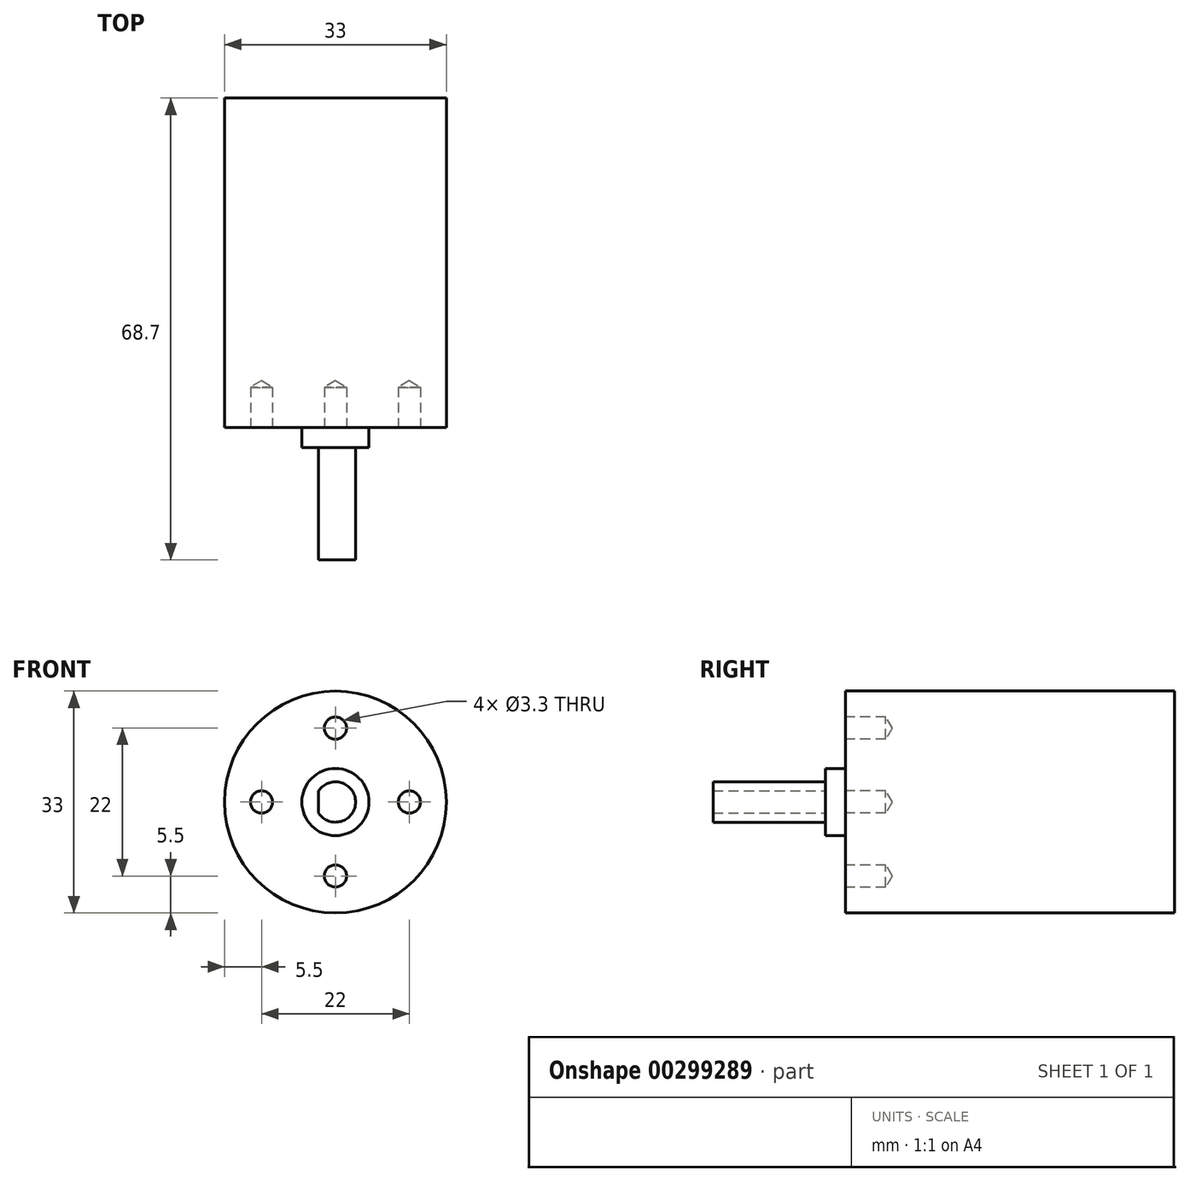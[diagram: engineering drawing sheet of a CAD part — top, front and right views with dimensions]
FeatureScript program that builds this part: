
annotation { "Feature Type Name" : "Feature", "Feature Type Description" : "" }
export const myFeature = defineFeature(function(context is Context, id is Id, definition is map)
    precondition{}
    {
        {
            var Q0;
            Q0=qCreatedBy(makeId("Front.planeOp"),FACE);
            var sketch = newSketch(context, id + "F0", { "sketchPlane" : qUnion([Q0])});
            skCircle(sketch, "E0", {"center": v(0, 0) * mm, "radius": 16.5 * mm});
            skSolve(sketch);
        }
        {
            var Q0;
            Q0=makeQuery(id+"F0.imprint","IMPRINT",FACE,{"disambiguationData":[TD([[makeQuery(id+"F0.imprint","IMPRINT",EDGE,{"derivedFrom":sQuery(id+"F0.wireOp",EDGE,"E0")}),1.0]])]});
            extrude(context, id + "F1", {"entities" : qUnion([Q0]), "depth" : 31.5 * mm});
        }
        {
            var Q0;
            Q0=makeQuery(id+"F1.opExtrude","CAP_FACE",FACE,{"disambiguationData":[OSD([sQuery(id+"F0.wireOp",EDGE,"E0")])],"isStart":true});
            extrude(context, id + "F2", {"entities" : qUnion([Q0]), "operationType" : NewBodyOperationType.ADD, "depth" : 17.5 * mm});
        }
        {
            var Q0;
            Q0=makeQuery(id+"F1.opExtrude","CAP_FACE",FACE,{"disambiguationData":[OSD([sQuery(id+"F0.wireOp",EDGE,"E0")])],"isStart":false});
            var sketch = newSketch(context, id + "F3", { "sketchPlane" : qUnion([Q0])});
            skCircle(sketch, "E1", {"center": v(0, 0) * mm, "radius": 8.5 * mm});
            skCircle(sketch, "E2", {"center": v(0, 0) * mm, "radius": 5 * mm});
            skCircle(sketch, "E3", {"center": v(0, 0) * mm, "radius": 3 * mm});
            skLineSegment(sketch, "E4", {"start": v(-2.5, 1.66) * mm, "end": v(-2.5, -1.66) * mm});
            skCircle(sketch, "E5", {"center": v(0, 11) * mm, "radius": 1.25 * mm});
            skCircle(sketch, "E6", {"center": v(11, 0) * mm, "radius": 1.25 * mm});
            skCircle(sketch, "E7", {"center": v(0, -11) * mm, "radius": 1.25 * mm});
            skCircle(sketch, "E8", {"center": v(-11, 0) * mm, "radius": 1.25 * mm});
            skSolve(sketch);
        }
        {
            var Q0;
            {var subQ0=sQuery(id+"F3.wireOp",EDGE,"E4");Q0=makeQuery(id+"F3.imprint","IMPRINT",FACE,{"disambiguationData":[TD([[makeQuery(id+"F3.imprint","IMPRINT",EDGE,{"derivedFrom":subQ0}),1.0]])]});}
            extrude(context, id + "F4", {"entities" : qUnion([Q0]), "operationType" : NewBodyOperationType.ADD, "depth" : 19.7 * mm});
        }
        {
            var Q0;
            Q0=makeQuery(id+"F3.imprint","IMPRINT",FACE,{"disambiguationData":[TD([[makeQuery(id+"F3.imprint","IMPRINT",EDGE,{"derivedFrom":sQuery(id+"F3.wireOp",EDGE,"E2")}),1.0]])]});
            var Q1;
            {var subQ0=sQuery(id+"F3.wireOp",EDGE,"E4");Q1=makeQuery(id+"F3.imprint","IMPRINT",FACE,{"disambiguationData":[TD([[makeQuery(id+"F3.imprint","IMPRINT",EDGE,{"derivedFrom":subQ0}),-1.0]])]});}
            extrude(context, id + "F5", {"entities" : qUnion([Q0, Q1]), "operationType" : NewBodyOperationType.ADD, "depth" : 3 * mm});
        }
        {
            var Q0;
            Q0=sQuery(id+"F3.wireOp",VERTEX,"E6.center");
            var Q1;
            Q1=sQuery(id+"F3.wireOp",VERTEX,"E7.center");
            var Q2;
            Q2=sQuery(id+"F3.wireOp",VERTEX,"E5.center");
            var Q3;
            Q3=sQuery(id+"F3.wireOp",VERTEX,"E8.center");
            var Q4;
            Q4=makeQuery(id+"F1.opExtrude","SWEPT_BODY",BODY,{"disambiguationData":[OSD([sQuery(id+"F0.wireOp",EDGE,"E0")])]});
            hole(context, id + "F6", {"style" : HoleStyle.SIMPLE, "endStyle" : HoleEndStyle.BLIND, "standardTappedOrClearance" : lookupTablePath({ "standard" : "ISO", "fit" : "Normal", "size" : "M3", "type" : "Clearance" }), "standardBlindInLast" : lookupTablePath({ "fit" : "Standard", "standard" : "ISO", "size" : "M3", "type" : "Clearance" }), "holeDiameter" : 3.3 * mm, "holeDepth" : 6 * mm, "tappedDepth" : 12.7 * mm, "tapClearance" : 3, "locations" : qUnion([Q0, Q1, Q2, Q3]), "scope" : qUnion([Q4])});
        }
    });
